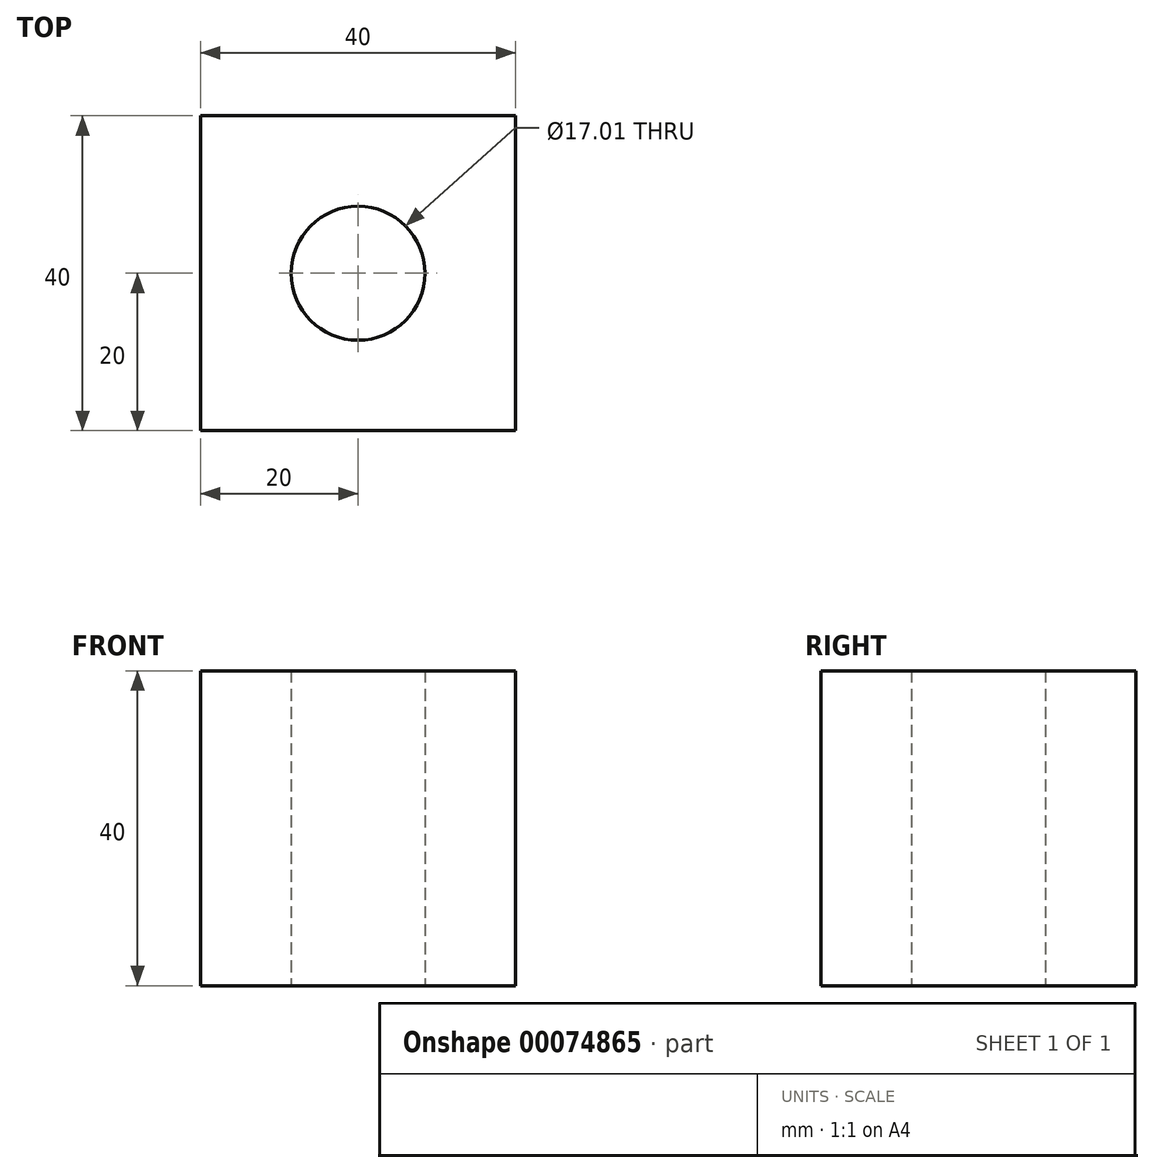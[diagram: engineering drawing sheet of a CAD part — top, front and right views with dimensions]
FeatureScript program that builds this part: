
annotation { "Feature Type Name" : "Feature", "Feature Type Description" : "" }
export const myFeature = defineFeature(function(context is Context, id is Id, definition is map)
    precondition{}
    {
        {
            var Q0;
            Q0=qCreatedBy(makeId("Top.planeOp"),FACE);
            var sketch = newSketch(context, id + "F0", { "sketchPlane" : qUnion([Q0])});
            skLineSegment(sketch, "E0.bottom", {"start": v(20, 20) * mm, "end": v(-20, 20) * mm});
            skLineSegment(sketch, "E0.top", {"start": v(20, -20) * mm, "end": v(-20, -20) * mm});
            skLineSegment(sketch, "E0.left", {"start": v(20, 20) * mm, "end": v(20, -20) * mm});
            skLineSegment(sketch, "E0.right", {"start": v(-20, 20) * mm, "end": v(-20, -20) * mm});
            skPoint(sketch, "E0.middle", {"position": v(0, 0) * mm});
            skCircle(sketch, "E1", {"center": v(0, 0) * mm, "radius": 8.5 * mm});
            skSolve(sketch);
        }
        {
            var Q0;
            Q0=makeQuery(id+"F0.imprint","IMPRINT",FACE,{"disambiguationData":[TD([[makeQuery(id+"F0.imprint","IMPRINT",EDGE,{"derivedFrom":sQuery(id+"F0.wireOp",EDGE,"E0.bottom")}),1.0]])]});
            extrude(context, id + "F1", {"entities" : qUnion([Q0]), "depth" : 40 * mm});
        }
    });
